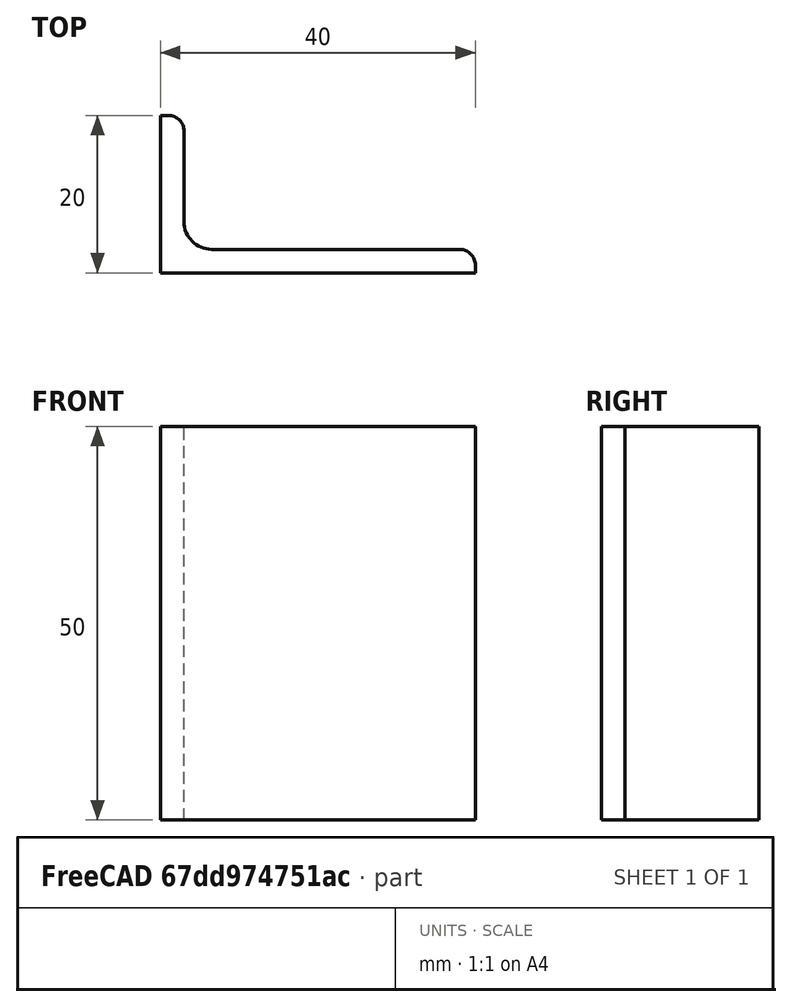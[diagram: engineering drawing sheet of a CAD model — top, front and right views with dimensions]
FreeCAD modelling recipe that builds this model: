
FCSTD DOCUMENT  (FreeCAD 0.15R4671 (Git))
Label: Angle Bar 40x20x3 EN10056 S235JR
License: All rights reserved
LicenseURL: http://en.wikipedia.org/wiki/All_rights_reserved
objects: Sketcher::SketchObject×1, Part::Extrusion×1
note: 2 computed .brp shape members not serialized (recipe doc carries the construction recipe); baked Part::Feature solids carry a one-line shape summary decoded from their .brp

FEATURE [Sketcher::SketchObject] Sketch
  sketch-geometry (9):
    g0: LineSegment StartX=0 StartY=0 StartZ=0 EndX=40 EndY=0 EndZ=0
    g1: LineSegment StartX=40 StartY=0 StartZ=0 EndX=40 EndY=1 EndZ=0
    g2: LineSegment StartX=38 StartY=3 StartZ=0 EndX=6.5 EndY=3 EndZ=0
    g3: LineSegment StartX=0 StartY=0 StartZ=0 EndX=0 EndY=20 EndZ=0
    g4: LineSegment StartX=0 StartY=20 StartZ=0 EndX=1 EndY=20 EndZ=0
    g5: LineSegment StartX=3 StartY=18 StartZ=0 EndX=3 EndY=6.5 EndZ=0
    g6: ArcOfCircle CenterX=6.5 CenterY=6.5 CenterZ=0 NormalX=0 NormalY=0 NormalZ=1 Radius=3.5 StartAngle=3.14159 EndAngle=4.71239
    g7: ArcOfCircle CenterX=1 CenterY=18 CenterZ=0 NormalX=0 NormalY=0 NormalZ=1 Radius=2 StartAngle=0 EndAngle=1.5708
    g8: ArcOfCircle CenterX=38 CenterY=1 CenterZ=0 NormalX=0 NormalY=0 NormalZ=1 Radius=2 StartAngle=0 EndAngle=1.5708
  constraints (23):
    c: Coincident(g0,g-1)
    c: Horizontal(g0)
    c: Coincident(g1,g0)
    c: Vertical(g1)
    c: Horizontal(g2)
    c: Coincident(g3,g-1)
    c: Vertical(g3)
    c: Coincident(g4,g3)
    c: Horizontal(g4)
    c: Vertical(g5)
    c: Tangent(g5,g6) = -1.5708
    c: Tangent(g2,g6) = 1.5708
    c: Tangent(g4,g7) = 1.5708
    c: Tangent(g5,g7) = 1.5708
    c: Tangent(g2,g8) = -1.5708
    c: Tangent(g1,g8) = -1.5708
    c: DistanceX(g0) = 40
    c: DistanceY(g3) = 20
    c: DistanceY(g0,g2) = 3
    c: DistanceX(g3,g5) = 3
    c: Radius(g6) = 3.5
    c: Radius(g8) = 2
    c: Radius(g7) = 2
FEATURE [Part::Extrusion] Extrude  label="Angle Bar 40x20x3 EN10056 S235JR"
  Base = -> Sketch
  Dir = (0,0,50)
  Solid = true
